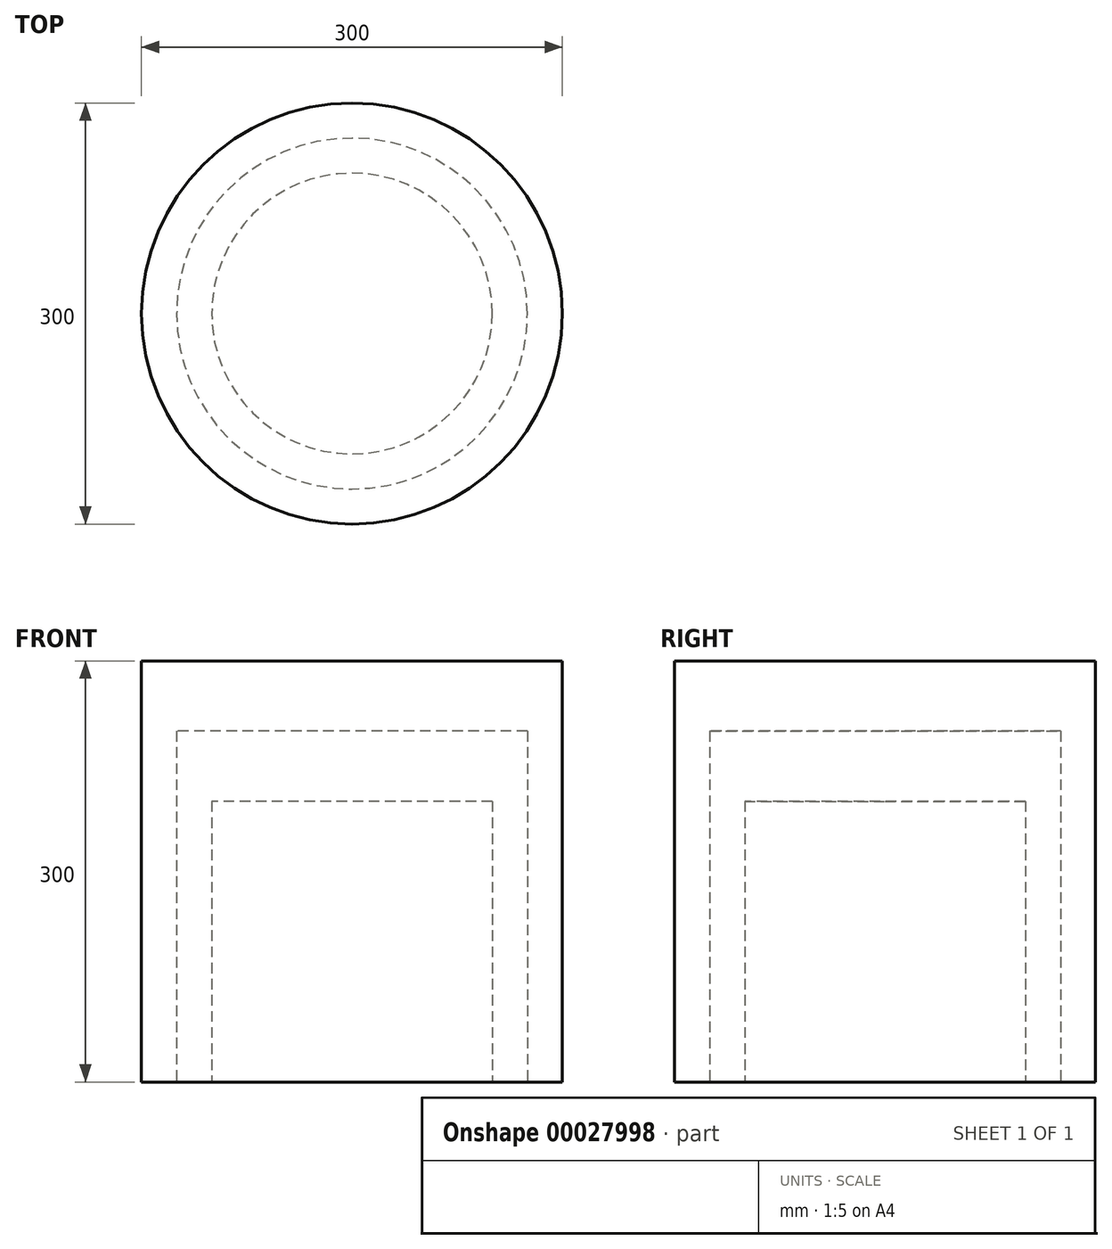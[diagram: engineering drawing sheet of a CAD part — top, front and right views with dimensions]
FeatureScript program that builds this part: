
annotation { "Feature Type Name" : "Feature", "Feature Type Description" : "" }
export const myFeature = defineFeature(function(context is Context, id is Id, definition is map)
    precondition{}
    {
        {
            var Q0;
            Q0=qCreatedBy(makeId("Top.planeOp"),FACE);
            var sketch = newSketch(context, id + "F0", { "sketchPlane" : qUnion([Q0])});
            skCircle(sketch, "E0", {"center": v(0, 0) * mm, "radius": 100 * mm});
            skCircle(sketch, "E1", {"center": v(0, 0) * mm, "radius": 125 * mm});
            skCircle(sketch, "E2", {"center": v(0, 0) * mm, "radius": 150 * mm});
            skSolve(sketch);
        }
        {
            var Q0;
            Q0=makeQuery(id+"F0.imprint","IMPRINT",FACE,{"disambiguationData":[TD([[makeQuery(id+"F0.imprint","IMPRINT",EDGE,{"derivedFrom":sQuery(id+"F0.wireOp",EDGE,"E0")}),1.0]])]});
            extrude(context, id + "F1", {"entities" : qUnion([Q0]), "depth" : 200 * mm});
        }
        {
            var Q0;
            Q0=makeQuery(id+"F0.imprint","IMPRINT",FACE,{"disambiguationData":[TD([[makeQuery(id+"F0.imprint","IMPRINT",EDGE,{"derivedFrom":sQuery(id+"F0.wireOp",EDGE,"E0")}),-1.0]])]});
            var Q1;
            Q1=makeQuery(id+"F0.imprint","IMPRINT",FACE,{"disambiguationData":[TD([[makeQuery(id+"F0.imprint","IMPRINT",EDGE,{"derivedFrom":sQuery(id+"F0.wireOp",EDGE,"E0")}),1.0]])]});
            extrude(context, id + "F2", {"entities" : qUnion([Q0, Q1]), "depth" : 250 * mm});
        }
        {
            var Q0;
            Q0=makeQuery(id+"F0.imprint","IMPRINT",FACE,{"disambiguationData":[TD([[makeQuery(id+"F0.imprint","IMPRINT",EDGE,{"derivedFrom":sQuery(id+"F0.wireOp",EDGE,"E1")}),-1.0]])]});
            var Q1;
            Q1=makeQuery(id+"F0.imprint","IMPRINT",FACE,{"disambiguationData":[TD([[makeQuery(id+"F0.imprint","IMPRINT",EDGE,{"derivedFrom":sQuery(id+"F0.wireOp",EDGE,"E0")}),-1.0]])]});
            var Q2;
            Q2=makeQuery(id+"F0.imprint","IMPRINT",FACE,{"disambiguationData":[TD([[makeQuery(id+"F0.imprint","IMPRINT",EDGE,{"derivedFrom":sQuery(id+"F0.wireOp",EDGE,"E0")}),1.0]])]});
            extrude(context, id + "F3", {"entities" : qUnion([Q0, Q1, Q2]), "depth" : 300 * mm});
        }
    });
